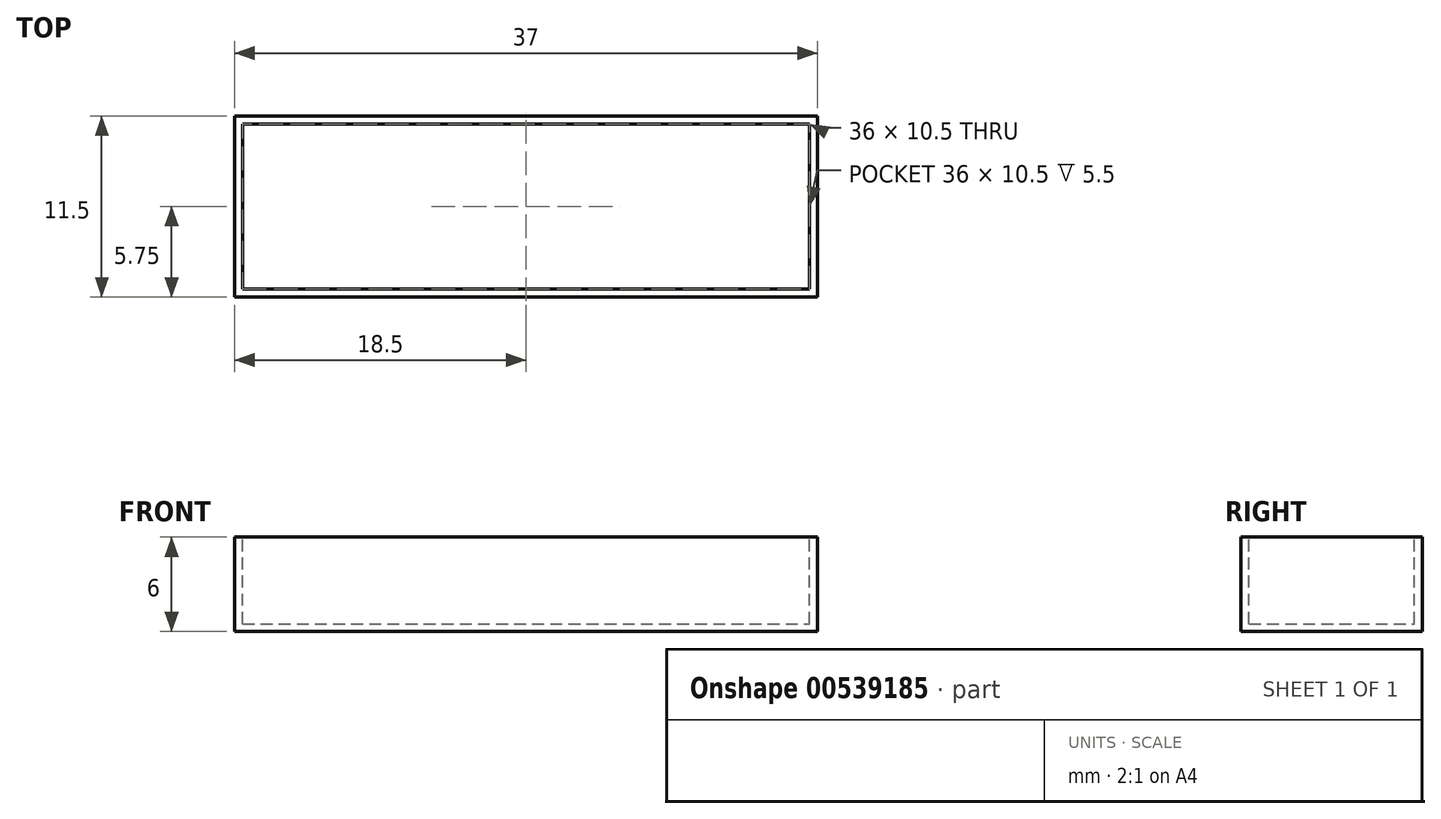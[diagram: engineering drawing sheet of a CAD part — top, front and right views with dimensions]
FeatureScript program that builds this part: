
annotation { "Feature Type Name" : "Feature", "Feature Type Description" : "" }
export const myFeature = defineFeature(function(context is Context, id is Id, definition is map)
    precondition{}
    {
        {
            var Q0;
            Q0=qCreatedBy(makeId("Top.planeOp"),FACE);
            var sketch = newSketch(context, id + "F0", { "sketchPlane" : qUnion([Q0])});
            skLineSegment(sketch, "E0.bottom", {"start": v(0, 0) * mm, "end": v(37, 0) * mm});
            skLineSegment(sketch, "E0.top", {"start": v(0, 11.5) * mm, "end": v(37, 11.5) * mm});
            skLineSegment(sketch, "E0.left", {"start": v(0, 0) * mm, "end": v(0, 11.5) * mm});
            skLineSegment(sketch, "E0.right", {"start": v(37, 0) * mm, "end": v(37, 11.5) * mm});
            skSolve(sketch);
        }
        {
            var Q0;
            Q0=qSketchRegion(id+"F0",true);
            extrude(context, id + "F1", {"entities" : qUnion([Q0]), "depth" : 6 * mm, "offsetDistance" : 25 * mm});
        }
        {
            var Q0;
            Q0=makeQuery(id+"F1.opExtrude","CAP_FACE",FACE,{"disambiguationData":[OSD([sQuery(id+"F0.wireOp",EDGE,"E0.bottom"),sQuery(id+"F0.wireOp",EDGE,"E0.top"),sQuery(id+"F0.wireOp",EDGE,"E0.left"),sQuery(id+"F0.wireOp",EDGE,"E0.right")])],"isStart":false});
            var sketch = newSketch(context, id + "F2", { "sketchPlane" : qUnion([Q0])});
            skLineSegment(sketch, "E1.bottom", {"start": v(0.5, 0.5) * mm, "end": v(36.5, 0.5) * mm});
            skLineSegment(sketch, "E1.top", {"start": v(0.5, 11) * mm, "end": v(36.5, 11) * mm});
            skLineSegment(sketch, "E1.left", {"start": v(0.5, 0.5) * mm, "end": v(0.5, 11) * mm});
            skLineSegment(sketch, "E1.right", {"start": v(36.5, 0.5) * mm, "end": v(36.5, 11) * mm});
            skSolve(sketch);
        }
        {
            var Q0;
            Q0=qSketchRegion(id+"F2",true);
            extrude(context, id + "F3", {"entities" : qUnion([Q0]), "operationType" : NewBodyOperationType.REMOVE, "oppositeDirection" : true, "depth" : 5.5 * mm, "offsetDistance" : 25 * mm});
        }
    });
